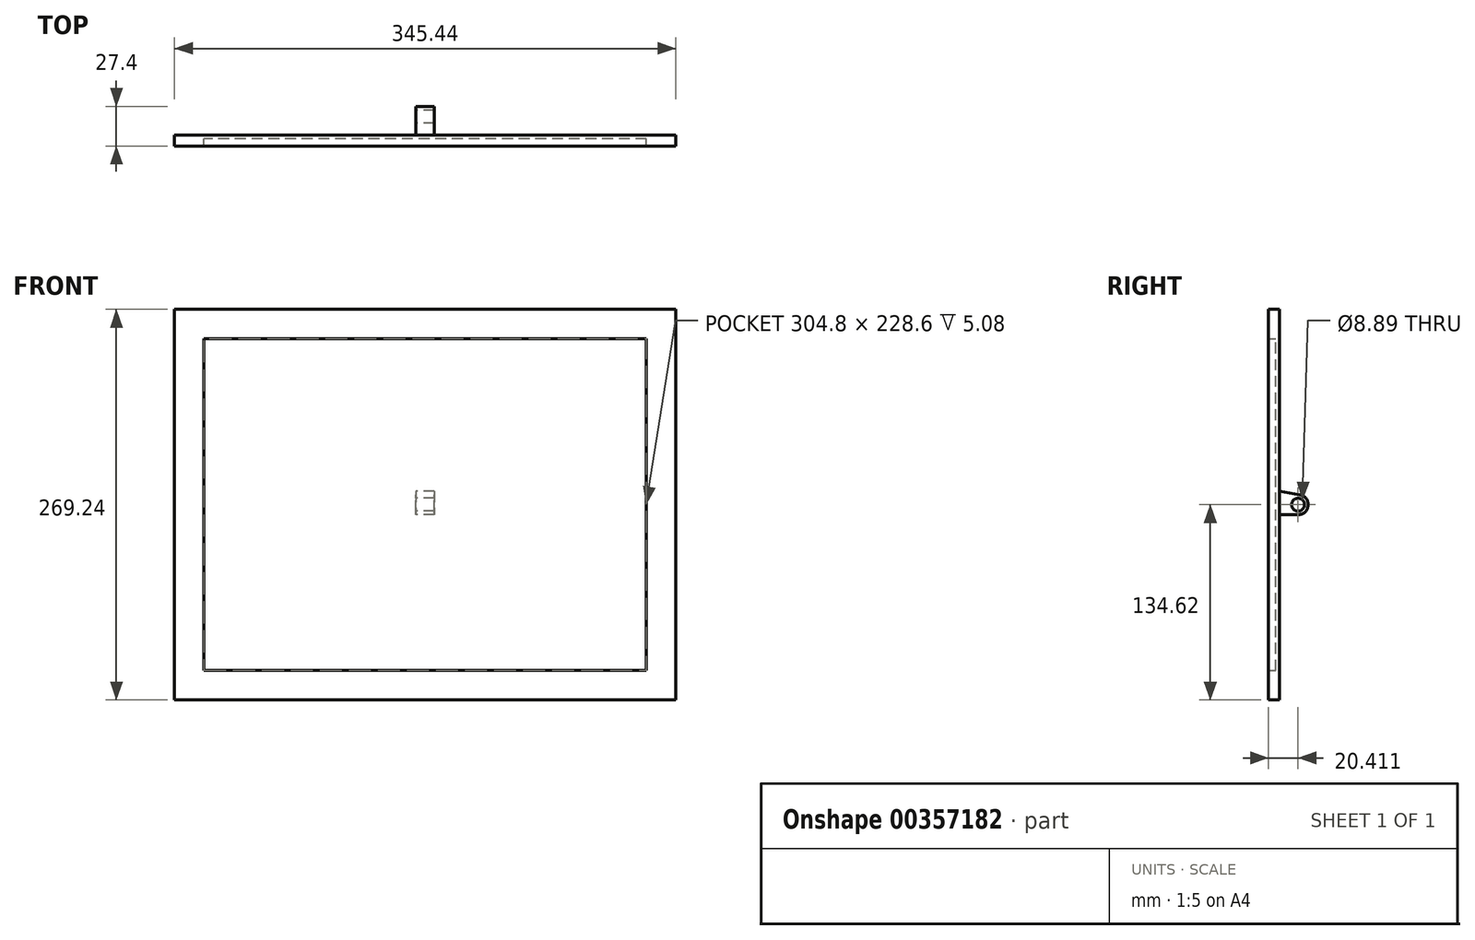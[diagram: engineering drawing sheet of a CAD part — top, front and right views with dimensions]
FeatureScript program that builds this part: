
annotation { "Feature Type Name" : "Feature", "Feature Type Description" : "" }
export const myFeature = defineFeature(function(context is Context, id is Id, definition is map)
    precondition{}
    {
        {
            var Q0;
            Q0=qCreatedBy(makeId("Front.planeOp"),FACE);
            var sketch = newSketch(context, id + "F0", { "sketchPlane" : qUnion([Q0])});
            skLineSegment(sketch, "E0.bottom", {"start": v(152.4, -114.3) * mm, "end": v(-152.4, -114.3) * mm});
            skLineSegment(sketch, "E0.top", {"start": v(152.4, 114.3) * mm, "end": v(-152.4, 114.3) * mm});
            skLineSegment(sketch, "E0.left", {"start": v(152.4, -114.3) * mm, "end": v(152.4, 114.3) * mm});
            skLineSegment(sketch, "E0.right", {"start": v(-152.4, -114.3) * mm, "end": v(-152.4, 114.3) * mm});
            skPoint(sketch, "E0.middle", {"position": v(0, 0) * mm});
            skLineSegment(sketch, "E1.0", {"start": v(-172.72, -134.62) * mm, "end": v(-172.72, 134.62) * mm});
            skLineSegment(sketch, "E1.1", {"start": v(172.72, -134.62) * mm, "end": v(-172.72, -134.62) * mm});
            skLineSegment(sketch, "E1.2", {"start": v(172.72, -134.62) * mm, "end": v(172.72, 134.62) * mm});
            skLineSegment(sketch, "E1.3", {"start": v(172.72, 134.62) * mm, "end": v(-172.72, 134.62) * mm});
            skSolve(sketch);
        }
        {
            var Q0;
            Q0=makeQuery(id+"F0.imprint","IMPRINT",FACE,{"disambiguationData":[TD([[makeQuery(id+"F0.imprint","IMPRINT",EDGE,{"derivedFrom":sQuery(id+"F0.wireOp",EDGE,"E0.bottom")}),-1.0]])]});
            extrude(context, id + "F1", {"entities" : qUnion([Q0]), "depth" : 2.54 * mm});
        }
        {
            var Q0;
            Q0=makeQuery(id+"F0.imprint","IMPRINT",FACE,{"disambiguationData":[TD([[makeQuery(id+"F0.imprint","IMPRINT",EDGE,{"derivedFrom":sQuery(id+"F0.wireOp",EDGE,"E0.bottom")}),1.0]])]});
            extrude(context, id + "F2", {"entities" : qUnion([Q0]), "operationType" : NewBodyOperationType.ADD, "depth" : 7.62 * mm});
        }
        {
            var Q0;
            Q0=qCreatedBy(makeId("Right.planeOp"),FACE);
            var sketch = newSketch(context, id + "F3", { "sketchPlane" : qUnion([Q0])});
            skCircle(sketch, "E2", {"center": v(12.8, 0) * mm, "radius": 4.45 * mm});
            skLineSegment(sketch, "E3", {"start": v(0, 9.26) * mm, "end": v(0, -6.8) * mm});
            skCircle(sketch, "E4", {"center": v(12.8, 0) * mm, "radius": 6.99 * mm});
            skLineSegment(sketch, "E5", {"start": v(0, 9.26) * mm, "end": v(13.96, 6.89) * mm});
            skLineSegment(sketch, "E6", {"start": v(0, -6.8) * mm, "end": v(12.7, -6.98) * mm});
            skSolve(sketch);
        }
        {
            var Q0;
            Q0 = qSketchRegion(id + "F3", true);
            extrude(context, id + "F4", {"entities" : qUnion([Q0]), "operationType" : NewBodyOperationType.ADD, "endBound" : BoundingType.SYMMETRIC, "depth" : 12.7 * mm});
        }
    });
